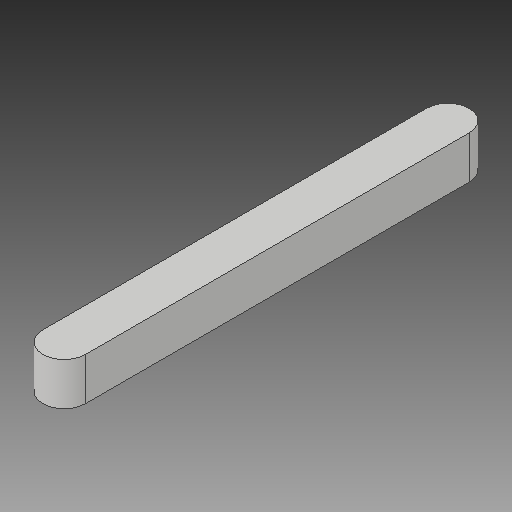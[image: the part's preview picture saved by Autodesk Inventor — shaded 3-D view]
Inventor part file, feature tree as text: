
AUTODESK INVENTOR PART (.ipt)
format: ipt  version: 2018 (Build 220112000, 112)  size: 78,848 bytes
history: native  units: in
note: dims shown in document units (in); Inventor stores cm internally (conversion verified against a paired STEP export)
features: fillet x1
ambient origin geometry x8: Origin, YZ Plane, XZ Plane, XY Plane, X Axis, Y Axis, Z Axis, Center Point
bodies: Solid1 (feature_tree)
feature tree (1):
  fillet  "Fillet1"  [1 undecoded]
note: 1 required parameter value undecoded (feature->parameter linkage not recoverable at this tier; creation-order binding heuristic only, values carry confidence <= 0.55)
